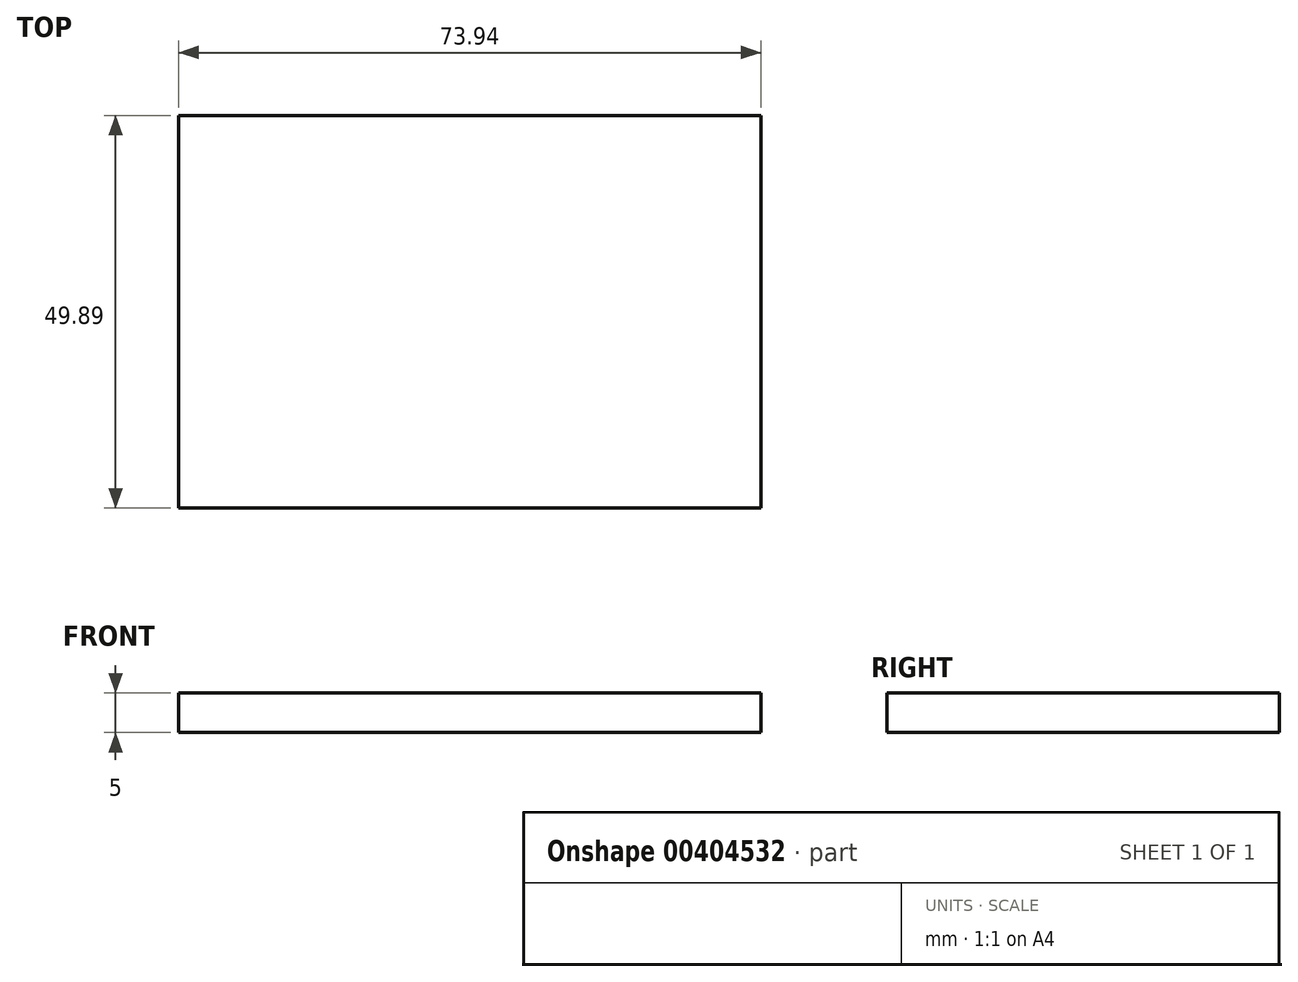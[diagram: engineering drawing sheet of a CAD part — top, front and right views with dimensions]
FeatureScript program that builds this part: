
annotation { "Feature Type Name" : "Feature", "Feature Type Description" : "" }
export const myFeature = defineFeature(function(context is Context, id is Id, definition is map)
    precondition{}
    {
        {
            var Q0;
            Q0=qCreatedBy(makeId("Top.planeOp"),FACE);
            var sketch = newSketch(context, id + "F0", { "sketchPlane" : qUnion([Q0])});
            skLineSegment(sketch, "E0.bottom", {"start": v(-39.26, 22.48) * mm, "end": v(34.68, 22.48) * mm});
            skLineSegment(sketch, "E0.top", {"start": v(-39.26, -27.4) * mm, "end": v(34.68, -27.4) * mm});
            skLineSegment(sketch, "E0.left", {"start": v(-39.26, 22.48) * mm, "end": v(-39.26, -27.4) * mm});
            skLineSegment(sketch, "E0.right", {"start": v(34.68, 22.48) * mm, "end": v(34.68, -27.4) * mm});
            skSolve(sketch);
        }
        {
            var Q0;
            Q0 = qSketchRegion(id + "F0", true);
            extrude(context, id + "F1", {"entities" : qUnion([Q0]), "depth" : 5 * mm});
        }
    });
